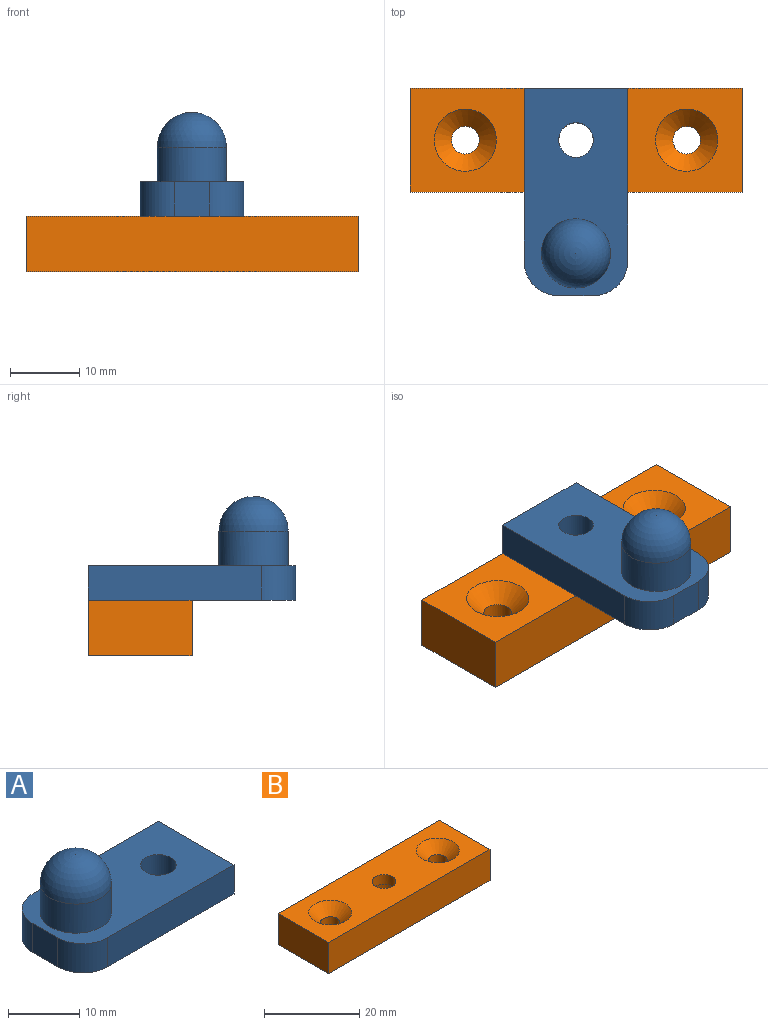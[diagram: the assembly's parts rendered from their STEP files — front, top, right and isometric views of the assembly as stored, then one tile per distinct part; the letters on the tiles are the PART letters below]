
ASSEMBLY  parts=2 mates=1
PART A: 11 faces, bbox 30x15x15 mm
  f0: plane 25x5mm, normal (0,1,0), area 125mm2, adj f3,f4,f5,f6
  f1: plane 5x5mm, normal (-1,0,0), area 25mm2, adj f4,f5,f6,f7
  f2: plane 25x5mm, normal (0,-1,0), area 125mm2, adj f3,f4,f5,f7
  f3: plane 15x5mm, normal (1,0,0), area 75mm2, adj f0,f2,f4,f5
  f4: plane 30x15mm, normal (0,0,1), area 341.1mm2, adj f0,f1,f2,f3,f6,f7,f8,f10
  f5: plane 30x15mm, normal (0,0,-1), area 419.6mm2, adj f0,f1,f2,f3,f6,f7,f10
  f6: cylinder r=5mm len=5mm, axis (0,0,1), area 39.3mm2, adj f0,f1,f4,f5
  f7: cylinder r=5mm len=5mm, axis (0,0,-1), area 39.3mm2, adj f1,f2,f4,f5
  f8: cylinder r=5mm len=10mm, axis (0,0,-1), area 157.1mm2, adj f4,f9
  f9: sphere r=5mm, area 157.1mm2, adj f8
  f10: cylinder r=2.5mm len=5mm, axis (0,0,1), area 78.5mm2, adj f4,f5
PART B: 13 faces, bbox 48x15x8 mm
  f0: plane 48x8mm, normal (0,1,0), area 384mm2, adj f1,f3,f4,f5
  f1: plane 15x8mm, normal (-1,0,0), area 120mm2, adj f0,f2,f4,f5
  f2: plane 48x8mm, normal (0,-1,0), area 384mm2, adj f1,f3,f4,f5
  f3: plane 15x8mm, normal (1,0,0), area 120mm2, adj f0,f2,f4,f5
  f4: plane 48x15mm, normal (0,0,1), area 573.1mm2, adj f0,f1,f2,f3,f6,f10,f12
  f5: plane 48x15mm, normal (0,0,-1), area 642.1mm2, adj f0,f1,f2,f3,f8,f9,f11
  f6: cylinder r=2.5mm len=5mm, axis (0,0,-1), area 39.3mm2, adj f4,f7
  f7: plane 8.2x8.2mm, normal (0,0,-1), area 33.2mm2, adj f6,f8
  f8: cylinder r=4.1mm len=8.2mm, axis (0,0,-1), area 141.7mm2, adj f5,f7
  f9: cylinder r=2mm len=5.5mm, axis (0,0,1), area 69.1mm2, adj f5,f10
  f10: cone r=2mm half-angle=45deg, axis (0,0,1), area 72.2mm2, adj f4,f9
  f11: cylinder r=2mm len=5.5mm, axis (0,0,1), area 69.1mm2, adj f5,f12
  f12: cone r=2mm half-angle=45deg, axis (0,0,1), area 72.2mm2, adj f4,f11
PLACE A rot(axis=(0,0,1),90deg) t=(0.23,-7.47,3.84)mm
PLACE B t=(0.24,0.03,-4.16)mm fixed
MATE revolute B.f6 <-> A.f10  axis (0,0,1) through (0.24,0.03,3.84)mm
